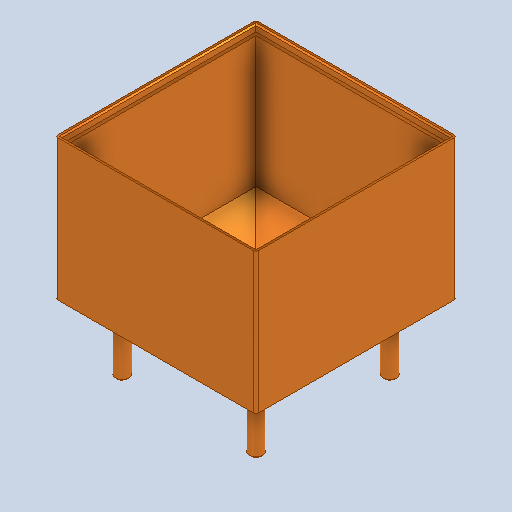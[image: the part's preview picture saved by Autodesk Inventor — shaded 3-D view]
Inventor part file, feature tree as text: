
AUTODESK INVENTOR PART (.ipt)
format: ipt  version: 2023 (Build 270158000, 158)  size: 397,824 bytes
history: native  units: mm
features: sketch x7, extrude x5, chamfer x2, plane x1, loft x1, shell x1, hole x1, fillet x1, other x1
ambient origin geometry x8: Origin, YZ Plane, XZ Plane, XY Plane, X Axis, Y Axis, Z Axis, Center Point
bodies: Solid1 (feature_tree)
feature tree (20):
  extrude  "Extrusion1"  Depth=150.0mm
  extrude  "Extrusion2"  Depth=75.0mm
  plane  "Work Plane1"
  loft  "Loft1"
  shell  "Shell2"  Thickness=140.0mm
  hole  "Hole1"  [1 undecoded]
  extrude  "Extrusion3"  Depth=50.0mm
  extrude  "Extrusion4"  TaperAngle=0.0deg  [1 undecoded]
  chamfer  "Chamfer1"  Angle=90.0deg  [1 undecoded]
  extrude  "Extrusion5"  Depth=2.0mm TaperAngle=0.0deg
  chamfer  "Chamfer2"  Distance=2.5mm
  fillet  "Fillet1"  Radius=2.5mm
  sketch  "Sketch1"  dims[d0=150.0mm d1=150.0mm]
  sketch  "Sketch2"  dims[d4=100.0mm d5=0.0mm d6=75.0mm]
  sketch  "Sketch3"  dims[d7=75.0mm d8=140.0mm d9=140.0mm]
  other  "Edges1"
  sketch  "Sketch6"  dims[d10=5.0mm d11=5.0mm]
  sketch  "Sketch8"  dims[d12=90.0mm d13=0.0mm d14=50.0mm]
  sketch  "Sketch9"  dims[d15=30.0mm d16=0.0mm d17=90.0deg d18=0.0mm d19=90.0deg]
  sketch  "Sketch10"  dims[d21=5.0mm d22=50.0mm d23=6.0mm d24=4.0mm d25=2.0mm d26=90.0deg d27=8.0mm d28=20.594885mm d29=5.0mm d30=0.0mm d31=2.5mm d32=2.5mm d33=5.0mm d34=0.0mm d35=1.0mm d36=2.0mm d37=45.0deg d38=10.0mm d39=50.0mm d40=10.0mm d41=10.0mm d42=10.0mm d43=0.0mm d44=0.0mm d45=1.0mm d46=2.0mm d47=45.0deg d48=2.0mm d49=0.375mm]
note: 3 required parameter values undecoded (feature->parameter linkage not recoverable at this tier; creation-order binding heuristic only, values carry confidence <= 0.55)
